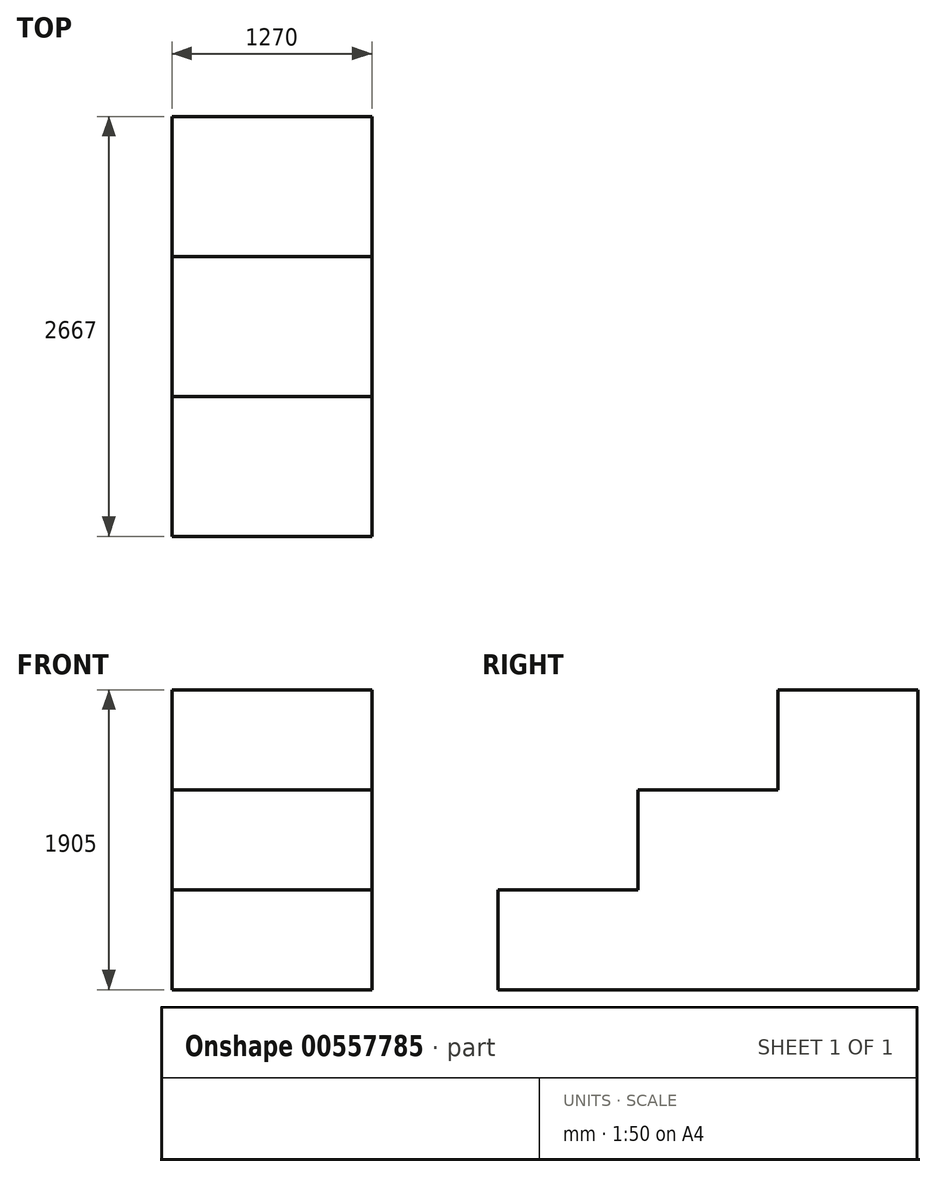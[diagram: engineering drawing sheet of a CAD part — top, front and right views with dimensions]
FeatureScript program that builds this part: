
annotation { "Feature Type Name" : "Feature", "Feature Type Description" : "" }
export const myFeature = defineFeature(function(context is Context, id is Id, definition is map)
    precondition{}
    {
        {
            var Q0;
            Q0=qCreatedBy(makeId("Front.planeOp"),FACE);
            var sketch = newSketch(context, id + "F0", { "sketchPlane" : qUnion([Q0])});
            skLineSegment(sketch, "E0", {"start": v(-70.57, -40.6) * mm, "end": v(1199.43, -40.6) * mm});
            skLineSegment(sketch, "E1", {"start": v(1199.43, -40.6) * mm, "end": v(1199.43, 594.4) * mm});
            skLineSegment(sketch, "E2", {"start": v(1199.43, 594.4) * mm, "end": v(-70.57, 594.4) * mm});
            skLineSegment(sketch, "E3", {"start": v(-70.57, 594.4) * mm, "end": v(-70.57, -40.6) * mm});
            skLineSegment(sketch, "E4", {"start": v(1199.43, 594.4) * mm, "end": v(1199.43, 1229.4) * mm});
            skLineSegment(sketch, "E5", {"start": v(1199.43, 1229.4) * mm, "end": v(-70.57, 1229.4) * mm});
            skLineSegment(sketch, "E6", {"start": v(-70.57, 1229.4) * mm, "end": v(-70.57, 594.4) * mm});
            skLineSegment(sketch, "E7", {"start": v(1199.43, 1229.4) * mm, "end": v(1199.43, 1864.4) * mm});
            skLineSegment(sketch, "E8", {"start": v(1199.43, 1864.4) * mm, "end": v(-70.57, 1864.4) * mm});
            skLineSegment(sketch, "E9", {"start": v(-70.57, 1864.4) * mm, "end": v(-70.57, 1229.4) * mm});
            skSolve(sketch);
        }
        {
            var Q0;
            Q0=makeQuery(id+"F0.imprint","IMPRINT",FACE,{"disambiguationData":[TD([[makeQuery(id+"F0.imprint","IMPRINT",EDGE,{"derivedFrom":sQuery(id+"F0.wireOp",EDGE,"E0")}),1.0]])]});
            var Q1;
            Q1=makeQuery(id+"F0.imprint","IMPRINT",FACE,{"disambiguationData":[TD([[makeQuery(id+"F0.imprint","IMPRINT",EDGE,{"derivedFrom":sQuery(id+"F0.wireOp",EDGE,"E2")}),-1.0]])]});
            var Q2;
            Q2=makeQuery(id+"F0.imprint","IMPRINT",FACE,{"disambiguationData":[TD([[makeQuery(id+"F0.imprint","IMPRINT",EDGE,{"derivedFrom":sQuery(id+"F0.wireOp",EDGE,"E5")}),-1.0]])]});
            extrude(context, id + "F1", {"entities" : qUnion([Q0, Q1, Q2]), "oppositeDirection" : true, "depth" : 2667 * mm, "offsetDistance" : 25.4 * mm});
        }
        {
            var Q0;
            Q0=makeQuery(id+"F1.opExtrude","SWEPT_FACE",FACE,{"disambiguationData":[OSD([sQuery(id+"F0.wireOp",EDGE,"E8")])]});
            var sketch = newSketch(context, id + "F2", { "sketchPlane" : qUnion([Q0])});
            skLineSegment(sketch, "E10", {"start": v(-70.57, 2667) * mm, "end": v(-70.57, 0) * mm});
            skLineSegment(sketch, "E11", {"start": v(-70.57, 0) * mm, "end": v(1199.43, 0) * mm});
            skLineSegment(sketch, "E12", {"start": v(1199.43, 0) * mm, "end": v(1199.43, 889) * mm});
            skLineSegment(sketch, "E13", {"start": v(1199.43, 889) * mm, "end": v(-70.57, 889) * mm});
            skLineSegment(sketch, "E14", {"start": v(1199.43, 889) * mm, "end": v(1199.43, 1778) * mm});
            skLineSegment(sketch, "E15", {"start": v(1199.43, 1778) * mm, "end": v(-70.57, 1778) * mm});
            skLineSegment(sketch, "E16", {"start": v(-70.57, 1778) * mm, "end": v(-70.57, 889) * mm});
            skLineSegment(sketch, "E17", {"start": v(1199.43, 1778) * mm, "end": v(1199.43, 2667) * mm});
            skLineSegment(sketch, "E18", {"start": v(1199.43, 2667) * mm, "end": v(-70.57, 2667) * mm});
            skSolve(sketch);
        }
        {
            var Q0;
            Q0=makeQuery(id+"F2.imprint","IMPRINT",FACE,{"disambiguationData":[TD([[makeQuery(id+"F2.imprint","IMPRINT",EDGE,{"derivedFrom":sQuery(id+"F2.wireOp",EDGE,"E13")}),-1.0]])]});
            extrude(context, id + "F3", {"entities" : qUnion([Q0]), "operationType" : NewBodyOperationType.REMOVE, "oppositeDirection" : true, "depth" : 635 * mm, "offsetDistance" : 25.4 * mm});
        }
        {
            var Q0;
            {var subQ1=sQuery(id+"F0.wireOp",EDGE,"E8");Q0=makeQuery(id+"F3.boolean.opBoolean","SPLIT",FACE,{"disambiguationData":[TD([makeQuery(id+"F3.opExtrude","SWEPT_FACE",FACE,{"disambiguationData":[OSD([sQuery(id+"F2.wireOp",EDGE,"E13")])]})])],"derivedFrom":makeQuery(id+"F1.opExtrude","SWEPT_FACE",FACE,{"disambiguationData":[OSD([subQ1])]})});}
            extrude(context, id + "F4", {"entities" : qUnion([Q0]), "operationType" : NewBodyOperationType.REMOVE, "oppositeDirection" : true, "depth" : 1270 * mm, "offsetDistance" : 25.4 * mm});
        }
    });
